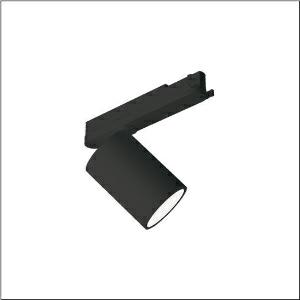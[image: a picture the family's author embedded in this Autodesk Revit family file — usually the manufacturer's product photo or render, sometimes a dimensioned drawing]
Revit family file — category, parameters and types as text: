
# Revit family: spot_31_51sf33mad4b
name_source: partatom
category: Lighting Fixtures
units: mm (PartAtom-declared; Revit-internal decimal feet)

## family parameters
Cut with Voids When Loaded = No
Host = Face
Light Source = No
Part Type = Normal
Room Calculation Point = No
Round Connector Dimension = Use Diameter
Shared = No

## types (1)
- --- (1 x LED, 5190 lm, 41.5 W, 4000K)
    Apparent Load = 42 VA
    CIE Flux Codes = 92 97 99 100 100
    Color Rendering = 90
    Color Temperature = 4000K
    Default Elevation = 1800 mm
    Description = Spot 31, directional spotlight, light control with lens, of PMMA, LED rated luminous flux: 4.980lm, light colour: 940, control gear: ECG Multilumen, with 3-phase adapter, mains connection: 220..240V, AC, 50/60Hz, of aluminium, jet black (RAL 9005), length: 213mm, diameter: 90mm, protection rating (complete): IP20, insulation class (complete): insulation class I (protective earthing), certification: CE, impact resistance: IK02, permissible ambient temperature for indoor applications: -20..+40°C, packaging unit: 1 piece
    Height = 175 mm
    Lamp = 1 x LED
    Lamp Light Flux = 5190 lm
    Lamp Power = 41.5 W
    Lamp count = 1
    Length = 90 mm
    Luminous efficacy = 125 lm/W
    Manufacturer = Siteco
    ModVariant = No
    Model = 51SF33MAD4B
    Mounting Place = Ceiling
    Mounting Type = Pendant
    Number of Poles = 1
    OnlyDefault = Yes
    Power Factor = 1
    Product Name = Spot 31
    Product group = directional spotlight
    ProductGroupID = 905
    Protection Class = Protection class I
    Protection Degree = IP 20
    RLX_Detail_Level = 1
    RLX_Emergency_Light_Flux = 0 lm
    RLX_Emergency_Type = 0
    RLX_Emergency_Type_DB = No
    RlxData = <blob elided: 20877 chars, md5=8b16b152>
    Socket = socket
    Standby Power = 0 W
    System Light Flux = 5190 lm
    System Power = 42 W
    Type Comments = factory setting: luminous flux: 100 % | (ON | ON | ON | ON) | 1050 mA
    Type Image = l_1273723.jpg
    URL = http://relux.com
    VarID = @adj_096019
    Voltage = 0 V
    Weight = 0.00 kg
    Width = 0 mm  [stored 0 ft]

note: [stored X ft] marks values corroborated as IEEE doubles in the binary element streams (Revit-internal decimal feet)

## geometry (parser evidence)
native form markers: Blend x4, Sweep x11
no freeform markers — native parametric forms only
